# Revit family: PRD_AR_FlshCntrlDvcs_F3SWcFlushingValve_F3SF40011
name_source: partatom
category: Plumbing Fixtures
units: mm (PartAtom-declared; Revit-internal decimal feet)

## family parameters
Cut with Voids When Loaded = Yes
Enable Cutting in Views = Yes
Host = Face
Maintain Annotation Orientation = No
OmniClass Number = 23.45.05.14.99
OmniClass Title = Other Sanitary Washing Plumbing Fixtures
Part Type = Normal
Room Calculation Point = No
Round Connector Dimension = Use Diameter
Shared = No

## types (1)
- F3SF4001
    AssetType = Fixed
    BIMObjectName = PRD_AR_FlushControlDevices_F3SWcFlushingValve_F3SF4001
    BasicColour = Stainless steel-look
    BodyMaterial = PRD_AR_StainlessSteel_Brushed
    BottomMaterial = PRD_AR_ChromatedBrass_HighPolished
    CW Connection = Yes
    CWFU = 0
    Category = Pr_75_50_46_31, Flush control devices
    CloseOffRating = 0.0 Pa
    Color = Stainless steel-look
    DN = 20 mm  [stored 0.0656168 ft]
    Default Elevation = 1219 mm
    Description = F3S WC flushing valve DN 20, for wall-mounted toilet bowls, fitting group 1, with remote control for concealed mounting. Especially suitable for facilities at risk of vandalism. Self-closing upper component for remote operation, hydraulically controlled, piston-free design, automatic and backlash-free closing. Automatic flush flow regulation and adjustable flush water volume. Flush valve complete with flush pipe connection and screw connection. All-metal construction, visible parts polished chromium-plated. Stainless steel cover plate 190 x 245 x 2 mm for invisible mounting via threaded rods, up to a wall thickness of 50 to 500 mm, pre-mounted push-button actuation, flush-mounted box. Hydraulic control lines and empty conduit (2 m) and mounting material. Connection and maintenance via service room.
    DiameterNominal = DN 20
    Export Type to IFC As = IfcValveType
    Features = All-metal construction, visible parts polished chromium-plated. Stainless steel cover plate 190 x 245 x 2 mm.
    Finish = Satin finished
    Flow = 0.0 L/s
    FlowCoefficient = 0
    FlushingRate = 0.0 L/s
    FunctionalPrinciple = Hydraulic self-closing
    HW Connection = Yes
    HWFU = 0
    IfcExportAs = IfcValveType
    IfcExportType = FLUSHING
    IsHighPressure = No
    Manufacturer = KWC Group Management AG
    ManufacturerName = KWC Group Management AG
    ManufacturerURL = www.kwc-professional.com
    Material = Stainless steel
    MaterialCasing = Stainless steel
    MaterialCodeCasing = 1.4301 Chrome Nickel steel V2A
    MaterialFitting = Brass-look
    Model = F3SF4001
    ModelNumber = 2030068191
    ModelReference = F3SF4001
    NBSDescription = Flush control devices
    NBSReference = 90-15-35/470
    Name = F3S WC flushing valve F3SF4001
    NominalDepth = 2 mm  [stored 0.00656168 ft]
    NominalHeight = 245 mm  [stored 0.803806 ft]
    NominalWidth = 190 mm
    ProductInformation = http://pim.kwc.com
    ProtectiveShutdown = No
    Size = 20
    Status = New
    SurfaceFinishCasing = Satin finished
    TestPressure = 0.0 Pa
    Type IFC Predefined Type = FLUSHING
    TypeOfFlushingFitting = WC flush valve
    TypeOfMounting = Concealed
    TypeOfOperation = Manual operation
    URL = www.kwc-professional.com
    Uniclass2015Code = Pr_75_50_46_31
    Uniclass2015Title = Flush control devices
    Uniclass2015Version = Products v1.36
    ValveMechanism = OTHER
    ValveOperation = HYDRAULIC
    ValvePattern = OTHER
    Vent Connection = Yes
    Version = 1
    WFU = 0
    Waste Connection = Yes
    WorkingPressure = 0.0 Pa

note: [stored X ft] marks values corroborated as IEEE doubles in the binary element streams (Revit-internal decimal feet)

## geometry (parser evidence)
native form markers: Sweep x7
no freeform markers — native parametric forms only
